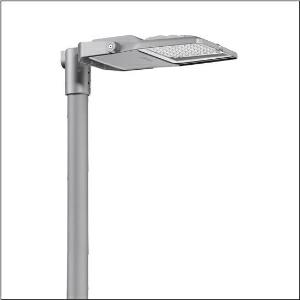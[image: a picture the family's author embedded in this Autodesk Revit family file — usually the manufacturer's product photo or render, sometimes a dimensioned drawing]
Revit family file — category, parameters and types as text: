
# Revit family: floodlight_fl_21_iq_mini___pl43_5xa7772d2a3a_1f0e
name_source: partatom
category: Lighting Fixtures
units: mm (PartAtom-declared; Revit-internal decimal feet)

## family parameters
Cut with Voids When Loaded = No
Host = Face
Light Source = No
Part Type = Normal
Room Calculation Point = No
Round Connector Dimension = Use Diameter
Shared = No

## types (1)
- --- (1 x LED, 18290 lm, 143 W, 3000K)
    Apparent Load = 143 VA
    CIE Flux Codes = 27 78 99 100 100
    Color Rendering = 70
    Color Temperature = 3000K
    Default Elevation = 1800 mm
    Description = Floodlight FL 21 iQ mini, floodlight, primary light control with lens, of PMMA, primary optical cover: protective disc, of toughened safety glass, transparent, light distribution: PL43, light emission: direct distribution, installation type: surface-mounted, LED, High Power LED, rated luminous flux: 18.290lm, luminous efficacy: 128lm/W, light colour: 730, colour temperature: 3000K, control: Auto-Match, Temp-Guard, Night-Set, Smart-Wire, Desk-Remote (wireless, voltage-free reading and setting of iQ features in the workshop via application-optimized NFC function/RFID function), optimised constant luminous flux control (CLO 2.0), Light-Fading, Lumen-Switch, with terminal, 6-pole, mains connection: 220..240V, AC, 50/60Hz, start of lifetime: 143W, end of service life: 152W, reduction: 61W, luminaire housing, of diecast aluminium, powder-coated, Siteco® metallic grey (DB 702S), corrosivity category C5 mid according to DIN EN ISO 12944, sealing non-destructively replaceable, please order mast flange separately, mast bracket, of steel, galvanised, powder-coated, protection rating (complete): IP66, insulation class (complete): insulation class II (safety insulation), certification: CE, ENEC, VDE, protection symbol: D, impact resistance: IK08, permissible operating ambient temperature: -40..+40°C, permissible operating ambient temperature for outdoor applications: -40..+50°C, standard: DIN EN 12944, LABS conformity tested according to VDMA 24364:2018-05, packaging unit: 1 piece

Light Distribution: PL43
    Height = 70 mm
    Lamp = 1 x LED
    Lamp Light Flux = 18290 lm
    Lamp Power = 143 W
    Lamp count = 1
    Length = 485 mm
    Luminous efficacy = 128 lm/W
    Manufacturer = Siteco
    ModVariant = No
    Model = 5XA7772D2A3A
    Number of Poles = 1
    OnlyDefault = Yes
    Power Factor = 1
    Product Name = Floodlight FL 21 iQ mini | PL43
    Product group = floodlight | pylon annexe
    ProductGroupID = 6200
    Protection Class = Protection class II
    Protection Degree = IP 66
    RLX_Detail_Level = 1
    RLX_Emergency_Light_Flux = 0 lm
    RLX_Emergency_Type = 0
    RLX_Emergency_Type_DB = No
    RlxData = <blob elided: 101341 chars, md5=13bf27f8>
    Socket = socket
    Standby Power = 0 W
    System Light Flux = 18290 lm
    System Power = 143 W
    Type Comments = factory setting: luminous flux: 100 % | dim-lin: 254 | 730 mA
    Type Image = l_1007125.jpg
    URL = http://relux.com
    VarID = @adj_093923
    Voltage = 0 V
    Weight = 0.00 kg
    Width = 337 mm

## geometry (parser evidence)
native form markers: Blend x4, Sweep x13
no freeform markers — native parametric forms only
